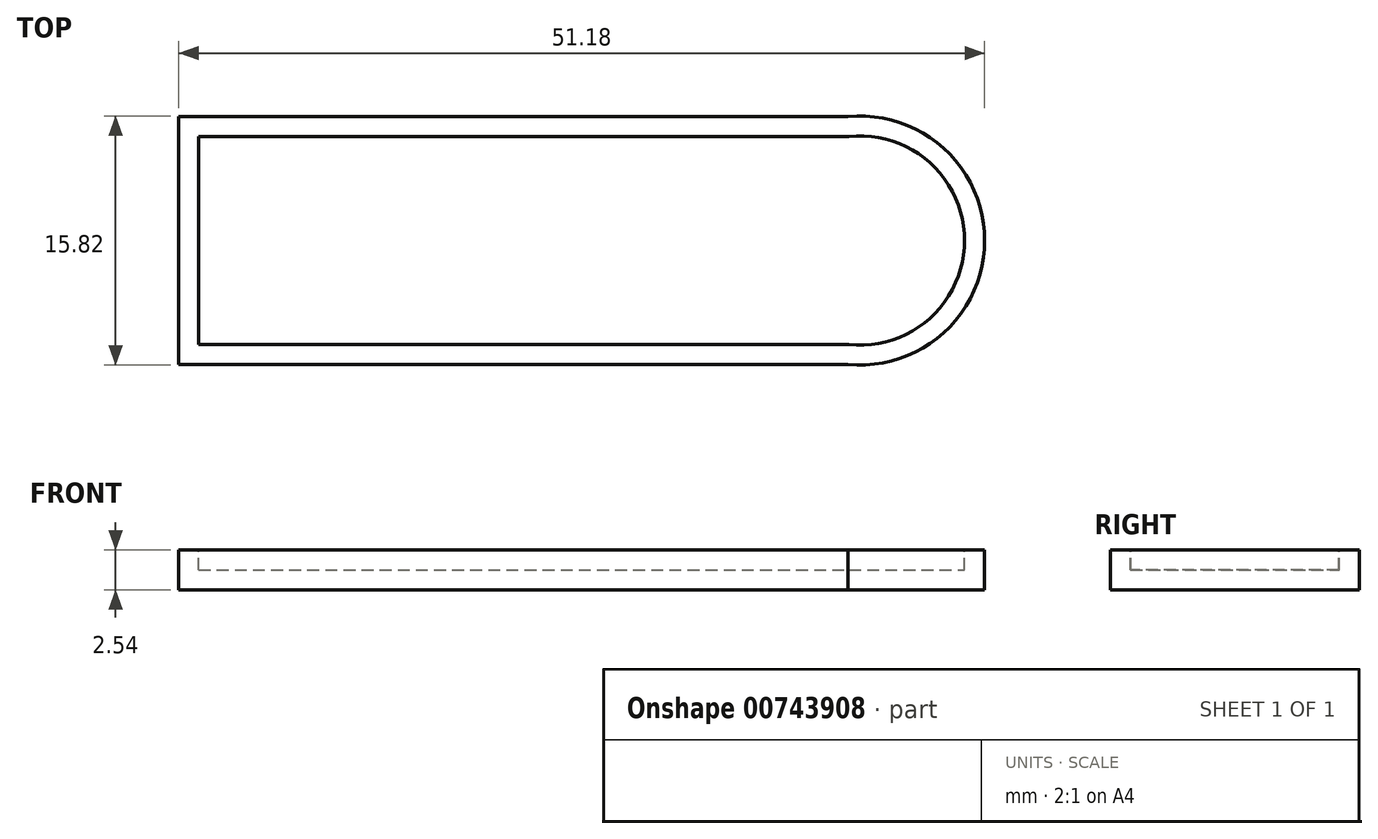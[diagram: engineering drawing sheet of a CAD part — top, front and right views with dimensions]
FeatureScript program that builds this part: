
annotation { "Feature Type Name" : "Feature", "Feature Type Description" : "" }
export const myFeature = defineFeature(function(context is Context, id is Id, definition is map)
    precondition{}
    {
        {
            var Q0;
            Q0=qCreatedBy(makeId("Top.planeOp"),FACE);
            var sketch = newSketch(context, id + "F0", { "sketchPlane" : qUnion([Q0])});
            skLineSegment(sketch, "E0.bottom", {"start": v(0, 0) * mm, "end": v(43.27, 0) * mm});
            skLineSegment(sketch, "E0.top", {"start": v(0, -15.74) * mm, "end": v(43.27, -15.74) * mm});
            skLineSegment(sketch, "E0.left", {"start": v(0, 0) * mm, "end": v(0, -15.74) * mm});
            skLineSegment(sketch, "E0.right", {"start": v(43.27, 0) * mm, "end": v(43.27, -15.74) * mm});
            skCircle(sketch, "E1", {"center": v(43.27, -7.87) * mm, "radius": 7.9 * mm});
            skSolve(sketch);
        }
        {
            var Q0;
            {var subQ1=sQuery(id+"F0.wireOp",EDGE,"E0.bottom");Q0=makeQuery(id+"F0.imprint","IMPRINT",FACE,{"disambiguationData":[TD([[makeQuery(id+"F0.imprint","IMPRINT",EDGE,{"derivedFrom":subQ1}),-1.0]])]});}
            var Q1;
            {var subQ0=sQuery(id+"F0.wireOp",EDGE,"E1");var subQ1=sQuery(id+"F0.wireOp",EDGE,"E0.right");var subQ2=makeQuery(id+"F0.imprint","INTERSECT",VERTEX,{"disambiguationData":[OD(0.0)],"derivedFrom":[subQ1,subQ0]});Q1=makeQuery(id+"F0.imprint","IMPRINT",FACE,{"disambiguationData":[TD([[makeQuery(id+"F0.imprint","IMPRINT",EDGE,{"disambiguationData":[TD([[subQ2,-1.0]])],"derivedFrom":subQ1}),1.0]])]});}
            var Q2;
            {var subQ0=sQuery(id+"F0.wireOp",EDGE,"E1");var subQ1=sQuery(id+"F0.wireOp",EDGE,"E0.right");var subQ2=makeQuery(id+"F0.imprint","INTERSECT",VERTEX,{"disambiguationData":[OD(0.0)],"derivedFrom":[subQ1,subQ0]});Q2=makeQuery(id+"F0.imprint","IMPRINT",FACE,{"disambiguationData":[TD([[makeQuery(id+"F0.imprint","IMPRINT",EDGE,{"disambiguationData":[TD([[subQ2,-1.0]])],"derivedFrom":subQ1}),-1.0]])]});}
            extrude(context, id + "F1", {"entities" : qUnion([Q0, Q1, Q2]), "depth" : -2.54 * mm, "offsetDistance" : 25.4 * mm});
        }
        {
            var Q0;
            Q0=makeQuery(id+"F1.opExtrude","CAP_FACE",FACE,{"disambiguationData":[OSD([sQuery(id+"F0.wireOp",EDGE,"E0.bottom"),sQuery(id+"F0.wireOp",EDGE,"E0.top"),sQuery(id+"F0.wireOp",EDGE,"E0.left"),sQuery(id+"F0.wireOp",EDGE,"E0.right"),sQuery(id+"F0.wireOp",EDGE,"E1")])],"isStart":true});
            shell(context, id + "F2", {"entities" : qUnion([Q0]), "thickness" : 1.27 * mm});
        }
    });
